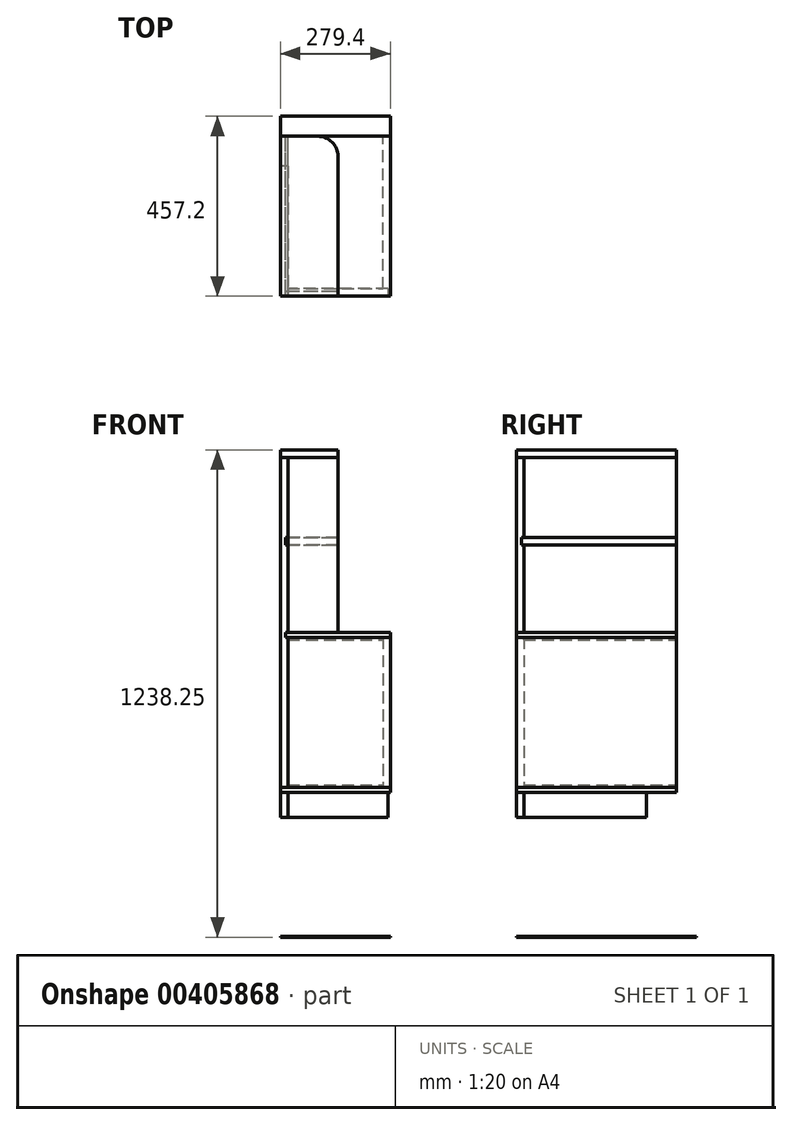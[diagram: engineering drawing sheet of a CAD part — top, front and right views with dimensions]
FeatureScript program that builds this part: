
annotation { "Feature Type Name" : "Feature", "Feature Type Description" : "" }
export const myFeature = defineFeature(function(context is Context, id is Id, definition is map)
    precondition{}
    {
        {
            var Q0;
            Q0=qCreatedBy(makeId("Front.planeOp"),FACE);
            var sketch = newSketch(context, id + "F0", { "sketchPlane" : qUnion([Q0])});
            skLineSegment(sketch, "E0.bottom", {"start": v(0, 368.3) * mm, "end": v(-19.05, 368.3) * mm});
            skLineSegment(sketch, "E0.top", {"start": v(0, 304.8) * mm, "end": v(-19.05, 304.8) * mm});
            skLineSegment(sketch, "E0.left", {"start": v(0, 368.3) * mm, "end": v(0, 304.8) * mm});
            skLineSegment(sketch, "E0.right", {"start": v(-19.05, 368.3) * mm, "end": v(-19.05, 304.8) * mm});
            skSolve(sketch);
        }
        {
            var Q0;
            Q0 = qSketchRegion(id + "F0", true);
            extrude(context, id + "F1", {"entities" : qUnion([Q0]), "oppositeDirection" : true, "depth" : 330.2 * mm});
        }
        {
            var Q0;
            Q0=makeQuery(id+"F1.opExtrude","SWEPT_FACE",FACE,{"disambiguationData":[OSD([sQuery(id+"F0.wireOp",EDGE,"E0.left")])]});
            var sketch = newSketch(context, id + "F2", { "sketchPlane" : qUnion([Q0])});
            skLineSegment(sketch, "E1.bottom", {"start": v(0, 368.3) * mm, "end": v(19.05, 368.3) * mm});
            skLineSegment(sketch, "E1.top", {"start": v(0, 304.8) * mm, "end": v(19.05, 304.8) * mm});
            skLineSegment(sketch, "E1.left", {"start": v(0, 368.3) * mm, "end": v(0, 304.8) * mm});
            skLineSegment(sketch, "E1.right", {"start": v(19.05, 368.3) * mm, "end": v(19.05, 304.8) * mm});
            skSolve(sketch);
        }
        {
            var Q0;
            Q0 = qSketchRegion(id + "F2", true);
            var Q1;
            Q1=sQuery(id+"F2.wireOp",EDGE,"E1.left");
            var Q2;
            Q2=sQuery(id+"F2.wireOp",EDGE,"E1.right");
            var Q3;
            Q3=sQuery(id+"F2.wireOp",EDGE,"E1.bottom");
            var Q4;
            Q4=sQuery(id+"F2.wireOp",EDGE,"E1.top");
            extrude(context, id + "F3", {"entities" : qUnion([Q0]), "surfaceEntities" : qUnion([Q1, Q2, Q3, Q4]), "depth" : 254 * mm});
        }
        {
            var Q0;
            Q0=makeQuery(id+"F1.opExtrude","SWEPT_FACE",FACE,{"disambiguationData":[OSD([sQuery(id+"F0.wireOp",EDGE,"E0.bottom")])]});
            var sketch = newSketch(context, id + "F4", { "sketchPlane" : qUnion([Q0])});
            skLineSegment(sketch, "E2.bottom", {"start": v(-19.05, 0) * mm, "end": v(260.35, 0) * mm});
            skLineSegment(sketch, "E2.top", {"start": v(-19.05, 406.4) * mm, "end": v(260.35, 406.4) * mm});
            skLineSegment(sketch, "E2.left", {"start": v(-19.05, 0) * mm, "end": v(-19.05, 406.4) * mm});
            skLineSegment(sketch, "E2.right", {"start": v(260.35, 0) * mm, "end": v(260.35, 406.4) * mm});
            skSolve(sketch);
        }
        {
            var Q0;
            Q0 = qSketchRegion(id + "F4", true);
            var Q1;
            Q1=sQuery(id+"F4.wireOp",EDGE,"E2.left");
            var Q2;
            Q2=sQuery(id+"F4.wireOp",EDGE,"E2.top");
            var Q3;
            Q3=sQuery(id+"F4.wireOp",EDGE,"E2.right");
            var Q4;
            Q4=sQuery(id+"F4.wireOp",EDGE,"E2.bottom");
            extrude(context, id + "F5", {"entities" : qUnion([Q0]), "surfaceEntities" : qUnion([Q1, Q2, Q3, Q4]), "depth" : 19.05 * mm});
        }
        {
            var Q0;
            Q0=makeQuery(id+"F5.opExtrude","SWEPT_FACE",FACE,{"disambiguationData":[OSD([sQuery(id+"F4.wireOp",EDGE,"E2.top")])]});
            var sketch = newSketch(context, id + "F6", { "sketchPlane" : qUnion([Q0])});
            skLineSegment(sketch, "E3.bottom", {"start": v(19.05, 387.35) * mm, "end": v(0, 387.35) * mm});
            skLineSegment(sketch, "E3.top", {"start": v(19.05, 381) * mm, "end": v(0, 381) * mm});
            skLineSegment(sketch, "E3.left", {"start": v(19.05, 387.35) * mm, "end": v(19.05, 381) * mm});
            skLineSegment(sketch, "E3.right", {"start": v(0, 387.35) * mm, "end": v(0, 381) * mm});
            skLineSegment(sketch, "E4.bottom", {"start": v(-260.35, 387.35) * mm, "end": v(-241.3, 387.35) * mm});
            skLineSegment(sketch, "E4.top", {"start": v(-260.35, 381) * mm, "end": v(-241.3, 381) * mm});
            skLineSegment(sketch, "E4.left", {"start": v(-260.35, 387.35) * mm, "end": v(-260.35, 381) * mm});
            skLineSegment(sketch, "E4.right", {"start": v(-241.3, 387.35) * mm, "end": v(-241.3, 381) * mm});
            skSolve(sketch);
        }
        {
            var Q0;
            Q0 = qSketchRegion(id + "F6", true);
            extrude(context, id + "F7", {"entities" : qUnion([Q0]), "operationType" : NewBodyOperationType.REMOVE, "endBound" : BoundingType.UP_TO_NEXT, "oppositeDirection" : true, "depth" : 25.4 * mm});
        }
        {
            var Q0;
            Q0=makeQuery(id+"F7.boolean.opBoolean","COPY",FACE,{"derivedFrom":makeQuery(id+"F7.opExtrude","SWEPT_FACE",FACE,{"disambiguationData":[OSD([sQuery(id+"F6.wireOp",EDGE,"E4.right")])]})});
            var sketch = newSketch(context, id + "F8", { "sketchPlane" : qUnion([Q0])});
            skLineSegment(sketch, "E5.bottom", {"start": v(0, 387.35) * mm, "end": v(19.05, 387.35) * mm});
            skLineSegment(sketch, "E5.top", {"start": v(0, 381) * mm, "end": v(19.05, 381) * mm});
            skLineSegment(sketch, "E5.left", {"start": v(0, 387.35) * mm, "end": v(0, 381) * mm});
            skLineSegment(sketch, "E5.right", {"start": v(19.05, 387.35) * mm, "end": v(19.05, 381) * mm});
            skSolve(sketch);
        }
        {
            var Q0;
            Q0=makeQuery(id+"F8.imprint","IMPRINT",FACE,{"disambiguationData":[TD([[makeQuery(id+"F8.imprint","IMPRINT",EDGE,{"derivedFrom":sQuery(id+"F8.wireOp",EDGE,"E5.bottom")}),-1.0]])]});
            extrude(context, id + "F9", {"entities" : qUnion([Q0]), "operationType" : NewBodyOperationType.REMOVE, "endBound" : BoundingType.UP_TO_NEXT, "oppositeDirection" : true, "depth" : 25.4 * mm});
        }
        {
            var Q0;
            Q0=makeQuery(id+"F9.boolean.opBoolean","MERGE",FACE,{"derivedFrom":[makeQuery(id+"F7.boolean.opBoolean","COPY",FACE,{"derivedFrom":makeQuery(id+"F7.opExtrude","SWEPT_FACE",FACE,{"disambiguationData":[OSD([sQuery(id+"F6.wireOp",EDGE,"E3.top")])]})}),makeQuery(id+"F7.boolean.opBoolean","COPY",FACE,{"derivedFrom":makeQuery(id+"F7.opExtrude","SWEPT_FACE",FACE,{"disambiguationData":[OSD([sQuery(id+"F6.wireOp",EDGE,"E4.top")])]})}),makeQuery(id+"F9.opExtrude","SWEPT_FACE",FACE,{"disambiguationData":[OSD([sQuery(id+"F8.wireOp",EDGE,"E5.top")])]})]});
            var sketch = newSketch(context, id + "F10", { "sketchPlane" : qUnion([Q0])});
            skLineSegment(sketch, "E6.bottom", {"start": v(260.35, 0) * mm, "end": v(241.3, 0) * mm});
            skLineSegment(sketch, "E6.top", {"start": v(260.35, 406.4) * mm, "end": v(241.3, 406.4) * mm});
            skLineSegment(sketch, "E6.left", {"start": v(260.35, 0) * mm, "end": v(260.35, 406.4) * mm});
            skLineSegment(sketch, "E6.right", {"start": v(241.3, 0) * mm, "end": v(241.3, 406.4) * mm});
            skLineSegment(sketch, "E7.bottom", {"start": v(0, 0) * mm, "end": v(241.3, 0) * mm});
            skLineSegment(sketch, "E7.top", {"start": v(0, 19.05) * mm, "end": v(241.3, 19.05) * mm});
            skLineSegment(sketch, "E7.left", {"start": v(0, 0) * mm, "end": v(0, 19.05) * mm});
            skLineSegment(sketch, "E7.right", {"start": v(241.3, 0) * mm, "end": v(241.3, 19.05) * mm});
            skSolve(sketch);
        }
        {
            var Q0;
            Q0 = qSketchRegion(id + "F10", true);
            extrude(context, id + "F11", {"entities" : qUnion([Q0]), "depth" : 381 * mm});
        }
        {
            var Q0;
            Q0=makeQuery(id+"F11.opExtrude","CAP_FACE",FACE,{"disambiguationData":[OSD([sQuery(id+"F10.wireOp",EDGE,"E6.bottom"),sQuery(id+"F10.wireOp",EDGE,"E6.top"),sQuery(id+"F10.wireOp",EDGE,"E6.left"),sQuery(id+"F10.wireOp",EDGE,"E6.right"),sQuery(id+"F10.wireOp",EDGE,"nJpbzDtH-quJb-x0EM-XHee-WdsqfySwf8nw.bottom"),sQuery(id+"F10.wireOp",EDGE,"nJpbzDtH-quJb-x0EM-XHee-WdsqfySwf8nw.top"),sQuery(id+"F10.wireOp",EDGE,"nJpbzDtH-quJb-x0EM-XHee-WdsqfySwf8nw.left"),sQuery(id+"F10.wireOp",EDGE,"nJpbzDtH-quJb-x0EM-XHee-WdsqfySwf8nw.right"),sQuery(id+"F10.wireOp",EDGE,"E7.bottom"),sQuery(id+"F10.wireOp",EDGE,"E7.top")])],"isStart":false});
            cPlane(context, id + "F12", {"entities" : qUnion([Q0]), "cplaneType" : CPlaneType.OFFSET, "offset" : 190.5 * mm, "oppositeDirection" : true, "width" : 152.4 * mm, "height" : 152.4 * mm});
        }
        {
            var Q0;
            Q0=makeQuery(id+"F5.opExtrude","SWEPT_BODY",BODY,{"disambiguationData":[OSD([sQuery(id+"F4.wireOp",EDGE,"E2.bottom"),sQuery(id+"F4.wireOp",EDGE,"E2.top"),sQuery(id+"F4.wireOp",EDGE,"E2.left"),sQuery(id+"F4.wireOp",EDGE,"E2.right")])]});
            var Q1;
            Q1=qCreatedBy(id+"F12.planeOp",FACE);
            mirror(context, id + "F13", {"entities" : qUnion([Q0]), "mirrorPlane" : qUnion([Q1])});
        }
        {
            var Q0;
            Q0=makeQuery(id+"F13.opPattern","COPY",FACE,{"derivedFrom":makeQuery(id+"F5.opExtrude","SWEPT_FACE",FACE,{"disambiguationData":[OSD([sQuery(id+"F4.wireOp",EDGE,"E2.top")])]}),"instanceName":"1"});
            var sketch = newSketch(context, id + "F14", { "sketchPlane" : qUnion([Q0])});
            skLineSegment(sketch, "E8.bottom", {"start": v(19.05, 774.7) * mm, "end": v(6.35, 774.7) * mm});
            skLineSegment(sketch, "E8.top", {"start": v(19.05, 762) * mm, "end": v(6.35, 762) * mm});
            skLineSegment(sketch, "E8.left", {"start": v(19.05, 774.7) * mm, "end": v(19.05, 762) * mm});
            skLineSegment(sketch, "E8.right", {"start": v(6.35, 774.7) * mm, "end": v(6.35, 762) * mm});
            skSolve(sketch);
        }
        {
            var Q0;
            Q0 = qSketchRegion(id + "F14", true);
            extrude(context, id + "F15", {"entities" : qUnion([Q0]), "operationType" : NewBodyOperationType.REMOVE, "endBound" : BoundingType.UP_TO_NEXT, "oppositeDirection" : true, "depth" : 25.4 * mm});
        }
        {
            var Q0;
            Q0=makeQuery(id+"F9.boolean.opBoolean","MERGE",FACE,{"derivedFrom":[makeQuery(id+"F7.boolean.opBoolean","COPY",FACE,{"derivedFrom":makeQuery(id+"F7.opExtrude","SWEPT_FACE",FACE,{"disambiguationData":[OSD([sQuery(id+"F6.wireOp",EDGE,"E3.top")])]})}),makeQuery(id+"F7.boolean.opBoolean","COPY",FACE,{"derivedFrom":makeQuery(id+"F7.opExtrude","SWEPT_FACE",FACE,{"disambiguationData":[OSD([sQuery(id+"F6.wireOp",EDGE,"E4.top")])]})}),makeQuery(id+"F9.opExtrude","SWEPT_FACE",FACE,{"disambiguationData":[OSD([sQuery(id+"F8.wireOp",EDGE,"E5.top")])]})]});
            var sketch = newSketch(context, id + "F16", { "sketchPlane" : qUnion([Q0])});
            skLineSegment(sketch, "E9.bottom", {"start": v(-19.05, 406.4) * mm, "end": v(0, 406.4) * mm});
            skLineSegment(sketch, "E9.top", {"start": v(-19.05, 0) * mm, "end": v(0, 0) * mm});
            skLineSegment(sketch, "E9.left", {"start": v(-19.05, 406.4) * mm, "end": v(-19.05, 0) * mm});
            skLineSegment(sketch, "E9.right", {"start": v(0, 406.4) * mm, "end": v(0, 0) * mm});
            skSolve(sketch);
        }
        {
            var Q0;
            Q0 = qSketchRegion(id + "F16", true);
            extrude(context, id + "F17", {"entities" : qUnion([Q0]), "depth" : 838.2 * mm});
        }
        {
            var Q0;
            Q0=makeQuery(id+"F13.opPattern","COPY",BODY,{"derivedFrom":makeQuery(id+"F5.opExtrude","SWEPT_BODY",BODY,{"disambiguationData":[OSD([sQuery(id+"F4.wireOp",EDGE,"E2.bottom"),sQuery(id+"F4.wireOp",EDGE,"E2.top"),sQuery(id+"F4.wireOp",EDGE,"E2.left"),sQuery(id+"F4.wireOp",EDGE,"E2.right")])]}),"instanceName":"1"});
            var Q1;
            Q1=makeQuery(id+"F17.opExtrude","SWEPT_BODY",BODY,{"disambiguationData":[OSD([sQuery(id+"F16.wireOp",EDGE,"E9.bottom"),sQuery(id+"F16.wireOp",EDGE,"E9.top"),sQuery(id+"F16.wireOp",EDGE,"E9.left"),sQuery(id+"F16.wireOp",EDGE,"E9.right")])]});
            booleanBodies(context, id + "F18", {"operationType" : BooleanOperationType.SUBTRACTION, "tools" : qUnion([Q0]), "targets" : qUnion([Q1]), "keepTools" : true});
        }
        {
            var Q0;
            Q0=makeQuery(id+"F17.opExtrude","SWEPT_FACE",FACE,{"disambiguationData":[OSD([sQuery(id+"F16.wireOp",EDGE,"E9.bottom")])]});
            var sketch = newSketch(context, id + "F19", { "sketchPlane" : qUnion([Q0])});
            skLineSegment(sketch, "E10.bottom", {"start": v(0, 1016) * mm, "end": v(6.35, 1016) * mm});
            skLineSegment(sketch, "E10.top", {"start": v(0, 996.95) * mm, "end": v(6.35, 996.95) * mm});
            skLineSegment(sketch, "E10.left", {"start": v(0, 1016) * mm, "end": v(0, 996.95) * mm});
            skLineSegment(sketch, "E10.right", {"start": v(6.35, 1016) * mm, "end": v(6.35, 996.95) * mm});
            skSolve(sketch);
        }
        {
            var Q0;
            Q0 = qSketchRegion(id + "F19", true);
            extrude(context, id + "F20", {"entities" : qUnion([Q0]), "operationType" : NewBodyOperationType.REMOVE, "endBound" : BoundingType.UP_TO_NEXT, "oppositeDirection" : true, "depth" : 25.4 * mm});
        }
        {
            var Q0;
            Q0=makeQuery(id+"F13.opPattern","COPY",FACE,{"derivedFrom":makeQuery(id+"F5.opExtrude","CAP_FACE",FACE,{"disambiguationData":[OSD([sQuery(id+"F4.wireOp",EDGE,"E2.bottom"),sQuery(id+"F4.wireOp",EDGE,"E2.top"),sQuery(id+"F4.wireOp",EDGE,"E2.left"),sQuery(id+"F4.wireOp",EDGE,"E2.right")])],"isStart":true}),"instanceName":"1"});
            var sketch = newSketch(context, id + "F21", { "sketchPlane" : qUnion([Q0])});
            skLineSegment(sketch, "E11.bottom", {"start": v(0, 0) * mm, "end": v(127, 0) * mm});
            skLineSegment(sketch, "E11.top", {"start": v(0, 19.05) * mm, "end": v(127, 19.05) * mm});
            skLineSegment(sketch, "E11.left", {"start": v(0, 0) * mm, "end": v(0, 19.05) * mm});
            skLineSegment(sketch, "E11.right", {"start": v(127, 0) * mm, "end": v(127, 19.05) * mm});
            skSolve(sketch);
        }
        {
            var Q0;
            Q0 = qSketchRegion(id + "F21", true);
            var Q1;
            Q1=makeQuery(id+"F17.opExtrude","CAP_FACE",FACE,{"disambiguationData":[OSD([sQuery(id+"F16.wireOp",EDGE,"E9.bottom"),sQuery(id+"F16.wireOp",EDGE,"E9.top"),sQuery(id+"F16.wireOp",EDGE,"E9.left"),sQuery(id+"F16.wireOp",EDGE,"E9.right")])],"isStart":false});
            extrude(context, id + "F22", {"entities" : qUnion([Q0]), "endBound" : BoundingType.UP_TO_SURFACE, "endBoundEntityFace" : qUnion([Q1]), "depth" : 25.4 * mm});
        }
        {
            var Q0;
            Q0=makeQuery(id+"F22.opExtrude","SWEPT_FACE",FACE,{"disambiguationData":[OSD([sQuery(id+"F21.wireOp",EDGE,"E11.right")])]});
            var sketch = newSketch(context, id + "F23", { "sketchPlane" : qUnion([Q0])});
            skLineSegment(sketch, "E12.bottom", {"start": v(19.05, 996.95) * mm, "end": v(12.7, 996.95) * mm});
            skLineSegment(sketch, "E12.top", {"start": v(19.05, 1016) * mm, "end": v(12.7, 1016) * mm});
            skLineSegment(sketch, "E12.left", {"start": v(19.05, 996.95) * mm, "end": v(19.05, 1016) * mm});
            skLineSegment(sketch, "E12.right", {"start": v(12.7, 996.95) * mm, "end": v(12.7, 1016) * mm});
            skSolve(sketch);
        }
        {
            var Q0;
            Q0 = qSketchRegion(id + "F23", true);
            extrude(context, id + "F24", {"entities" : qUnion([Q0]), "operationType" : NewBodyOperationType.REMOVE, "endBound" : BoundingType.UP_TO_NEXT, "oppositeDirection" : true, "depth" : 25.4 * mm});
        }
        {
            var Q0;
            Q0=makeQuery(id+"F24.boolean.opBoolean","COPY",FACE,{"derivedFrom":makeQuery(id+"F24.opExtrude","SWEPT_FACE",FACE,{"disambiguationData":[OSD([sQuery(id+"F23.wireOp",EDGE,"E12.bottom")])]})});
            var sketch = newSketch(context, id + "F25", { "sketchPlane" : qUnion([Q0])});
            skLineSegment(sketch, "E13.bottom", {"start": v(127, 12.7) * mm, "end": v(-6.35, 12.7) * mm});
            skLineSegment(sketch, "E13.top", {"start": v(127, 406.4) * mm, "end": v(-6.35, 406.4) * mm});
            skLineSegment(sketch, "E13.left", {"start": v(127, 12.7) * mm, "end": v(127, 406.4) * mm});
            skLineSegment(sketch, "E13.right", {"start": v(-6.35, 12.7) * mm, "end": v(-6.35, 406.4) * mm});
            skSolve(sketch);
        }
        {
            var Q0;
            Q0 = qSketchRegion(id + "F25", true);
            extrude(context, id + "F26", {"entities" : qUnion([Q0]), "depth" : 19.05 * mm});
        }
        {
            var Q0;
            Q0=makeQuery(id+"F17.opExtrude","CAP_FACE",FACE,{"disambiguationData":[OSD([sQuery(id+"F16.wireOp",EDGE,"E9.bottom"),sQuery(id+"F16.wireOp",EDGE,"E9.top"),sQuery(id+"F16.wireOp",EDGE,"E9.left"),sQuery(id+"F16.wireOp",EDGE,"E9.right")])],"isStart":false});
            var sketch = newSketch(context, id + "F27", { "sketchPlane" : qUnion([Q0])});
            skLineSegment(sketch, "E14.bottom", {"start": v(-19.05, 0) * mm, "end": v(127, 0) * mm});
            skLineSegment(sketch, "E14.top", {"start": v(-19.05, 406.4) * mm, "end": v(127, 406.4) * mm});
            skLineSegment(sketch, "E14.left", {"start": v(-19.05, 0) * mm, "end": v(-19.05, 406.4) * mm});
            skLineSegment(sketch, "E14.right", {"start": v(127, 0) * mm, "end": v(127, 406.4) * mm});
            skSolve(sketch);
        }
        {
            var Q0;
            Q0 = qSketchRegion(id + "F27", true);
            extrude(context, id + "F28", {"entities" : qUnion([Q0]), "depth" : 19.05 * mm});
        }
        {
            var Q0;
            Q0=qCreatedBy(makeId("Top.planeOp"),FACE);
            var sketch = newSketch(context, id + "F29", { "sketchPlane" : qUnion([Q0])});
            skLineSegment(sketch, "E15.bottom", {"start": v(-19.05, 0) * mm, "end": v(260.35, 0) * mm});
            skLineSegment(sketch, "E15.top", {"start": v(-19.05, 457.2) * mm, "end": v(260.35, 457.2) * mm});
            skLineSegment(sketch, "E15.left", {"start": v(-19.05, 0) * mm, "end": v(-19.05, 457.2) * mm});
            skLineSegment(sketch, "E15.right", {"start": v(260.35, 0) * mm, "end": v(260.35, 457.2) * mm});
            skSolve(sketch);
        }
        {
            var Q0;
            Q0 = qSketchRegion(id + "F29", true);
            var Q1;
            Q1 = qConstructionFilter(qBodyType(qCreatedBy(id + "F29" ,EDGE), BodyType.WIRE), ConstructionObject.NO);
            extrude(context, id + "F30", {"entities" : qUnion([Q0]), "surfaceEntities" : qUnion([Q1]), "depth" : 2.54 * mm});
        }
        {
            var Q0;
            Q0=makeQuery(id+"F28.opExtrude","CAP_FACE",FACE,{"disambiguationData":[OSD([sQuery(id+"F27.wireOp",EDGE,"E14.bottom"),sQuery(id+"F27.wireOp",EDGE,"E14.top"),sQuery(id+"F27.wireOp",EDGE,"E14.left"),sQuery(id+"F27.wireOp",EDGE,"E14.right")])],"isStart":false});
            var sketch = newSketch(context, id + "F31", { "sketchPlane" : qUnion([Q0])});
            skLineSegment(sketch, "E16.bottom", {"start": v(127, 406.4) * mm, "end": v(76.2, 406.4) * mm});
            skLineSegment(sketch, "E16.left", {"start": v(127, 406.4) * mm, "end": v(127, 355.6) * mm});
            skArc(sketch, "E17", {"start": v(127, 355.6) * mm, "mid": v(112.12, 391.52) * mm, "end": v(76.2, 406.4) * mm});
            skSolve(sketch);
        }
        {
            var Q0;
            Q0 = qSketchRegion(id + "F31", true);
            extrude(context, id + "F32", {"entities" : qUnion([Q0]), "operationType" : NewBodyOperationType.REMOVE, "oppositeDirection" : true, "depth" : 254 * mm});
        }
        {
            var Q0;
            Q0=makeQuery(id+"F26.opExtrude","SWEPT_BODY",BODY,{"disambiguationData":[OSD([sQuery(id+"F25.wireOp",EDGE,"E13.bottom"),sQuery(id+"F25.wireOp",EDGE,"E13.top"),sQuery(id+"F25.wireOp",EDGE,"E13.left"),sQuery(id+"F25.wireOp",EDGE,"E13.right")])]});
            var Q1;
            Q1=makeQuery(id+"F22.opExtrude","SWEPT_BODY",BODY,{"disambiguationData":[OSD([sQuery(id+"F21.wireOp",EDGE,"E11.bottom"),sQuery(id+"F21.wireOp",EDGE,"E11.top"),sQuery(id+"F21.wireOp",EDGE,"E11.left"),sQuery(id+"F21.wireOp",EDGE,"E11.right")])]});
            booleanBodies(context, id + "F33", {"operationType" : BooleanOperationType.SUBTRACTION, "tools" : qUnion([Q0]), "targets" : qUnion([Q1]), "keepTools" : true});
        }
    });
